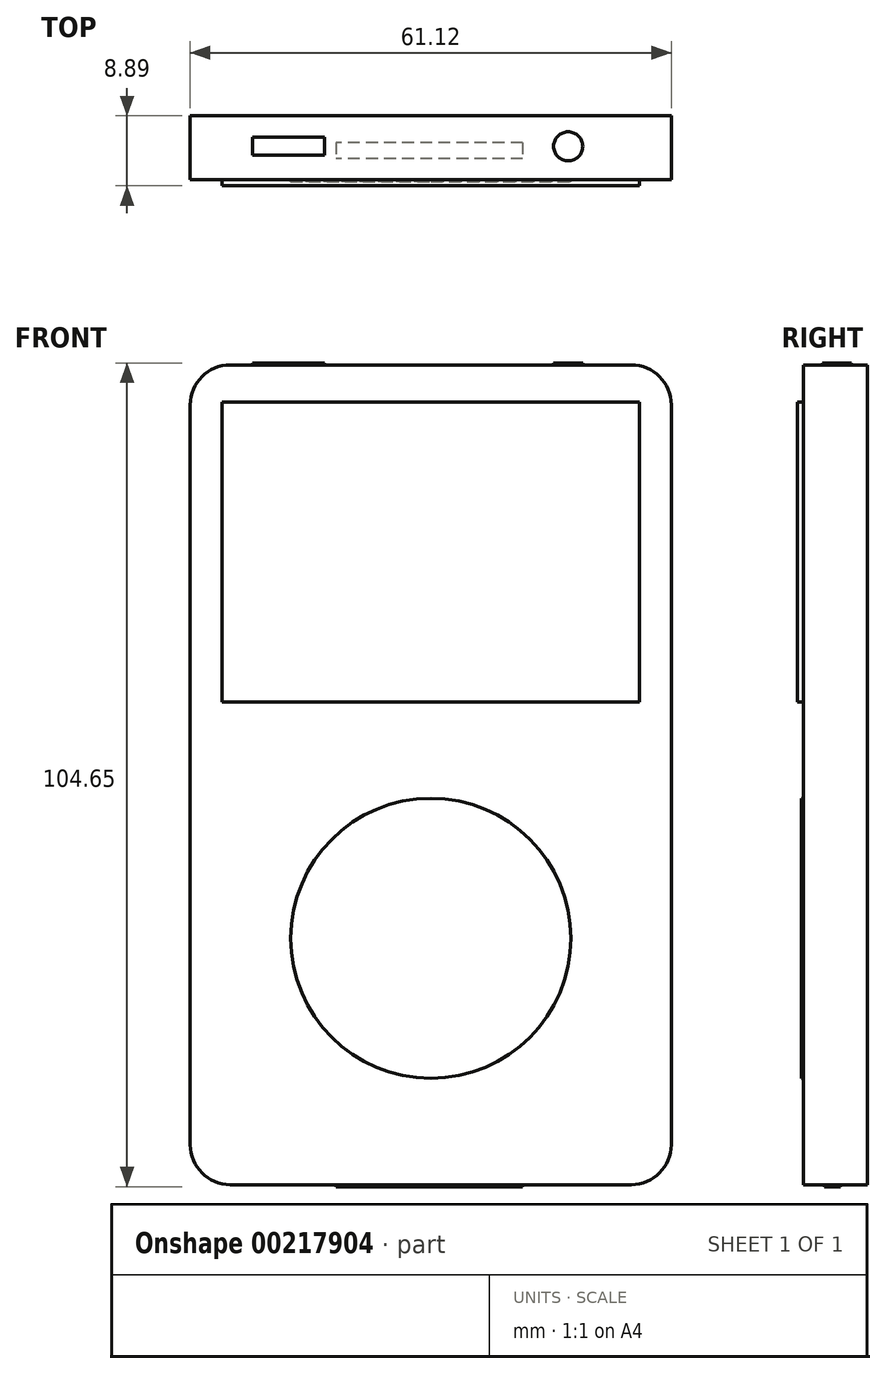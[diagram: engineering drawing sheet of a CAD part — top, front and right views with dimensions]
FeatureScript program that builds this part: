
annotation { "Feature Type Name" : "Feature", "Feature Type Description" : "" }
export const myFeature = defineFeature(function(context is Context, id is Id, definition is map)
    precondition{}
    {
        {
            var Q0;
            Q0=qCreatedBy(makeId("Front.planeOp"),FACE);
            var sketch = newSketch(context, id + "F0", { "sketchPlane" : qUnion([Q0])});
            skLineSegment(sketch, "E0.bottom", {"start": v(-50.17, 48.21) * mm, "end": v(10.95, 48.21) * mm});
            skLineSegment(sketch, "E0.top", {"start": v(-50.17, -55.93) * mm, "end": v(10.95, -55.93) * mm});
            skLineSegment(sketch, "E0.left", {"start": v(-50.17, 48.21) * mm, "end": v(-50.17, -55.93) * mm});
            skLineSegment(sketch, "E0.right", {"start": v(10.95, 48.21) * mm, "end": v(10.95, -55.93) * mm});
            skSolve(sketch);
        }
        {
            var Q0;
            Q0 = qSketchRegion(id + "F0", true);
            extrude(context, id + "F1", {"entities" : qUnion([Q0]), "depth" : 8.13 * mm});
        }
        {
            var Q0;
            Q0=makeQuery(id+"F1.opExtrude","SWEPT_EDGE",EDGE,{"disambiguationData":[OSD([sQuery(id+"F0.wireOp",EDGE,"E0.bottom"),sQuery(id+"F0.wireOp",EDGE,"E0.right")])]});
            var Q1;
            Q1=makeQuery(id+"F1.opExtrude","SWEPT_EDGE",EDGE,{"disambiguationData":[OSD([sQuery(id+"F0.wireOp",EDGE,"E0.bottom"),sQuery(id+"F0.wireOp",EDGE,"E0.left")])]});
            var Q2;
            Q2=makeQuery(id+"F1.opExtrude","SWEPT_EDGE",EDGE,{"disambiguationData":[OSD([sQuery(id+"F0.wireOp",EDGE,"E0.top"),sQuery(id+"F0.wireOp",EDGE,"E0.right")])]});
            var Q3;
            Q3=makeQuery(id+"F1.opExtrude","SWEPT_EDGE",EDGE,{"disambiguationData":[OSD([sQuery(id+"F0.wireOp",EDGE,"E0.top"),sQuery(id+"F0.wireOp",EDGE,"E0.left")])]});
            fillet(context, id + "F2", {"entities" : qUnion([Q0, Q1, Q2, Q3]), "radius" : 5.08 * mm, "tangentPropagation" : true, "allowEdgeOverflow" : false});
        }
        {
            var Q0;
            Q0=makeQuery(id+"F1.opExtrude","CAP_FACE",FACE,{"disambiguationData":[OSD([sQuery(id+"F0.wireOp",EDGE,"E0.bottom"),sQuery(id+"F0.wireOp",EDGE,"E0.top"),sQuery(id+"F0.wireOp",EDGE,"E0.left"),sQuery(id+"F0.wireOp",EDGE,"E0.right")])],"isStart":false});
            var sketch = newSketch(context, id + "F3", { "sketchPlane" : qUnion([Q0])});
            skCircle(sketch, "E1", {"center": v(-19.6, -24.62) * mm, "radius": 7.62 * mm});
            skCircle(sketch, "E2", {"center": v(-19.6, -24.62) * mm, "radius": 17.78 * mm});
            skLineSegment(sketch, "E3.bottom", {"start": v(6.9, 5.38) * mm, "end": v(-46.12, 5.38) * mm});
            skLineSegment(sketch, "E3.top", {"start": v(6.9, 43.48) * mm, "end": v(-46.12, 43.48) * mm});
            skLineSegment(sketch, "E3.left", {"start": v(6.9, 5.38) * mm, "end": v(6.9, 43.48) * mm});
            skLineSegment(sketch, "E3.right", {"start": v(-46.12, 5.38) * mm, "end": v(-46.12, 43.48) * mm});
            skPoint(sketch, "E3.middle", {"position": v(-19.6, 24.43) * mm});
            skSolve(sketch);
        }
        {
            var Q0;
            Q0=makeQuery(id+"F1.opExtrude","SWEPT_FACE",FACE,{"disambiguationData":[OSD([sQuery(id+"F0.wireOp",EDGE,"E0.bottom")])]});
            var sketch = newSketch(context, id + "F4", { "sketchPlane" : qUnion([Q0])});
            skCircle(sketch, "E4", {"center": v(-2.15, -3.88) * mm, "radius": 1.85 * mm});
            skLineSegment(sketch, "E5.bottom", {"start": v(-33.08, -5.02) * mm, "end": v(-42.24, -5.02) * mm});
            skLineSegment(sketch, "E5.top", {"start": v(-33.08, -2.73) * mm, "end": v(-42.24, -2.73) * mm});
            skLineSegment(sketch, "E5.left", {"start": v(-33.08, -5.02) * mm, "end": v(-33.08, -2.73) * mm});
            skLineSegment(sketch, "E5.right", {"start": v(-42.24, -5.02) * mm, "end": v(-42.24, -2.73) * mm});
            skPoint(sketch, "E5.middle", {"position": v(-37.66, -3.88) * mm});
            skLineSegment(sketch, "E6.0.0", {"start": v(-45.09, -8.13) * mm, "end": v(5.87, -8.13) * mm});
            skLineSegment(sketch, "E6.0.1", {"start": v(5.87, -8.13) * mm, "end": v(5.87, 0) * mm});
            skLineSegment(sketch, "E6.0.2", {"start": v(5.87, 0) * mm, "end": v(-45.09, 0) * mm});
            skLineSegment(sketch, "E6.0.3", {"start": v(-45.09, 0) * mm, "end": v(-45.09, -8.13) * mm});
            skSolve(sketch);
        }
        {
            var Q0;
            Q0=makeQuery(id+"F4.imprint","IMPRINT",FACE,{"disambiguationData":[TD([[makeQuery(id+"F4.imprint","IMPRINT",EDGE,{"derivedFrom":sQuery(id+"F4.wireOp",EDGE,"E5.bottom")}),-1.0]])]});
            var Q1;
            Q1=makeQuery(id+"F4.imprint","IMPRINT",FACE,{"disambiguationData":[TD([[makeQuery(id+"F4.imprint","IMPRINT",EDGE,{"derivedFrom":sQuery(id+"F4.wireOp",EDGE,"E4")}),1.0]])]});
            extrude(context, id + "F5", {"entities" : qUnion([Q0, Q1]), "operationType" : NewBodyOperationType.ADD, "depth" : 0.25 * mm});
        }
        {
            var Q0;
            Q0=makeQuery(id+"F1.opExtrude","SWEPT_FACE",FACE,{"disambiguationData":[OSD([sQuery(id+"F0.wireOp",EDGE,"E0.top")])]});
            var sketch = newSketch(context, id + "F6", { "sketchPlane" : qUnion([Q0])});
            skLineSegment(sketch, "E7.bottom", {"start": v(-7.94, 3.4) * mm, "end": v(-31.63, 3.4) * mm});
            skLineSegment(sketch, "E7.top", {"start": v(-7.94, 5.42) * mm, "end": v(-31.63, 5.42) * mm});
            skLineSegment(sketch, "E7.left", {"start": v(-7.94, 3.4) * mm, "end": v(-7.94, 5.42) * mm});
            skLineSegment(sketch, "E7.right", {"start": v(-31.63, 3.4) * mm, "end": v(-31.63, 5.42) * mm});
            skPoint(sketch, "E7.middle", {"position": v(-19.78, 4.41) * mm});
            skSolve(sketch);
        }
        {
            var Q0;
            Q0=makeQuery(id+"F6.imprint","IMPRINT",FACE,{"disambiguationData":[TD([[makeQuery(id+"F6.imprint","IMPRINT",EDGE,{"derivedFrom":sQuery(id+"F6.wireOp",EDGE,"E7.bottom")}),-1.0]])]});
            extrude(context, id + "F7", {"entities" : qUnion([Q0]), "operationType" : NewBodyOperationType.ADD, "depth" : 0.25 * mm});
        }
        {
            var Q0;
            Q0=makeQuery(id+"F3.imprint","IMPRINT",FACE,{"disambiguationData":[TD([[makeQuery(id+"F3.imprint","IMPRINT",EDGE,{"derivedFrom":sQuery(id+"F3.wireOp",EDGE,"E3.bottom")}),-1.0]])]});
            extrude(context, id + "F8", {"entities" : qUnion([Q0]), "operationType" : NewBodyOperationType.ADD, "depth" : 0.76 * mm});
        }
        {
            var Q0;
            Q0=makeQuery(id+"F3.imprint","IMPRINT",FACE,{"disambiguationData":[TD([[makeQuery(id+"F3.imprint","IMPRINT",EDGE,{"derivedFrom":sQuery(id+"F3.wireOp",EDGE,"E1")}),1.0]])]});
            extrude(context, id + "F9", {"entities" : qUnion([Q0]), "operationType" : NewBodyOperationType.ADD, "depth" : 0.25 * mm});
        }
        {
            var Q0;
            Q0=makeQuery(id+"F3.imprint","IMPRINT",FACE,{"disambiguationData":[TD([[makeQuery(id+"F3.imprint","IMPRINT",EDGE,{"derivedFrom":sQuery(id+"F3.wireOp",EDGE,"E1")}),-1.0]])]});
            extrude(context, id + "F10", {"entities" : qUnion([Q0]), "operationType" : NewBodyOperationType.ADD, "depth" : 0.25 * mm});
        }
        {
            var Q0;
            Q0=sQuery(id+"F3.wireOp",EDGE,"E1");
            extrude(context, id + "F11", {"bodyType" : ToolBodyType.SURFACE, "surfaceEntities" : qUnion([Q0]), "depth" : 0.5 * mm});
        }
    });
